# Revit family: Sanitary_Taps-And-Mixers_Sanindusa_Easy-Basin-Mixer-With-Medical-Lever
name_source: partatom
category: Plumbing Fixtures
revit_build: Autodesk Revit 2018 (Build: 20170223_1515(x64)
units: mm (PartAtom-declared; Revit-internal decimal feet)

## family parameters
Always vertical = Yes
Cut with Voids When Loaded = No
OmniClass Number = 23.45.00.00
OmniClass Title = Sanitary, Laundry, and Cleaning Equipment
Part Type = Normal
Room Calculation Point = No
Round Connector Dimension = Use Diameter
Shared = No
Work Plane-Based = No

## types (1)
- Sanitary_Taps-And-Mixers_Sanindusa_Easy-Basin-Mixer-With-Medical-Lever
    AssetType = Fixed
    BodyMaterial = Brass
    CartridgeType = D35 mm open ceramic cartridge
    Color = Silver
    Constituents = Single medical lever basin mixer. Fixing kit. 2 x M10x1-3/8 stainless steel flexible supply hoses. Pop up waste not available. Compatible with Unslotted waste for basins without overflow (ref-4V9711).
    Cost = 0 $
    Description = Easy basin mixer with medical lever
    Edition number = 1
    Element Type = FAUCET: A small diameter valve, with a free outlet, from which water is drawn.
    FaucetFunction = Mixed
    FaucetOperation = Other
    FaucetTopDescription = Single medical lever
    FaucetType = SprayMixing
    Features = Ceramic cartridge technology. Single lever mixer with medical lever for an easy access to persons with limited mobility.
    Finish = Chrome plated
    InletConnectionType = 2 x M10x1-3/8 stainless steel flexible supply hoses
    InstallationDate = 1900-12-31T23:59:59
    Manufacturer = Sanindusa
    ManufacturerName = Sanindusa
    ManufacturerURL = www.tec.sanindusa.pt
    Material = Brass
    ModelNumber = 536830111
    ModelReference = Easy
    Name = Easy basin mixer with medical lever
    NominalHeight = 243 mm
    NominalLength = 47 mm  [stored 0.154199 ft]
    NominalWidth = 158 mm
    OperatingMechanismMaterial = Brass
    Pre-defined type (IFC) = FAUCET
    Product Guid = 74e983fe-0b09-47a1-9b0c-b5a78794dcf9
    Product data url = https://bimobject.com
    ProductInformation = https://www.tec.sanindusa.pt
    ProductionYear = 2017
    Size = 47x158x243
    Type (IFC) = IfcValveType
    URL = www.tec.sanindusa.pt
    Uniclass2015Version = Products v1.6
    ValveMechanism = UNSET
    ValveOperation = OTHER
    ValvePattern = UNSET
    Version = 2
    WarrantyDescription = https://www.tec.sanindusa.pt
    WarrantyDurationParts = 5
    WarrantyDurationUnit = year
    WarrantyStartDate = 1900-12-31T23:59:59
1900-12-31T23:59:59
    Weight = 1.50 kg

note: [stored X ft] marks values corroborated as IEEE doubles in the binary element streams (Revit-internal decimal feet)

## geometry (parser evidence)
native form markers: Sweep x6
no freeform markers — native parametric forms only
